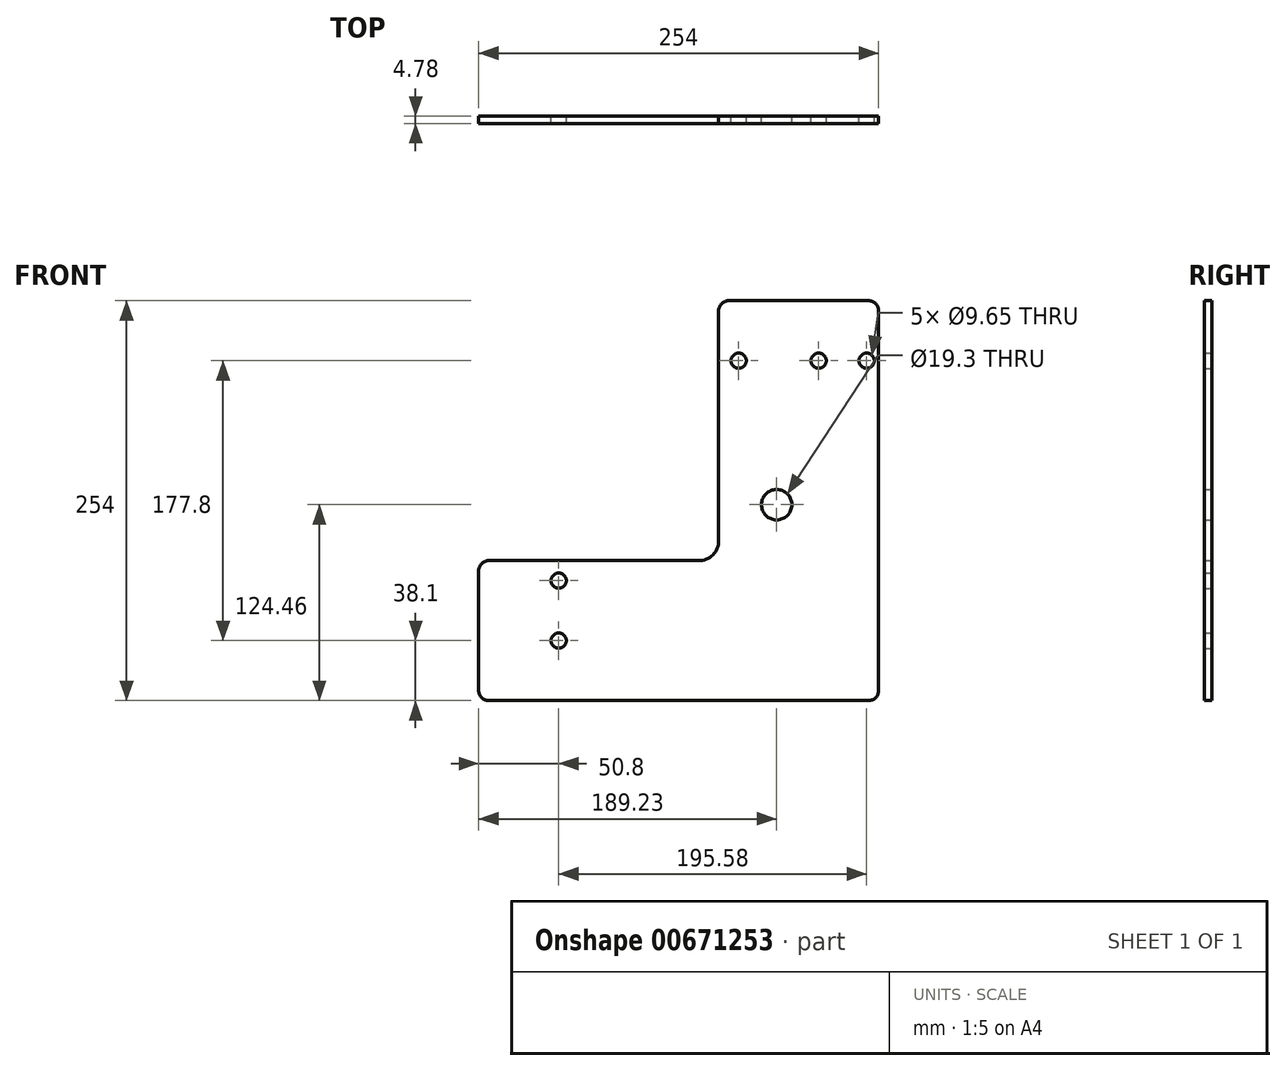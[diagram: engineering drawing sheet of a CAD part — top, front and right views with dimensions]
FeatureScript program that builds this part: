
annotation { "Feature Type Name" : "Feature", "Feature Type Description" : "" }
export const myFeature = defineFeature(function(context is Context, id is Id, definition is map)
    precondition{}
    {
        {
            var Q0;
            Q0=qCreatedBy(makeId("Front.planeOp"),FACE);
            var sketch = newSketch(context, id + "F0", { "sketchPlane" : qUnion([Q0])});
            skPoint(sketch, "E0.middle", {"position": v(0, 0) * mm});
            skLineSegment(sketch, "E1", {"start": v(0, 6.35) * mm, "end": v(0, 247.65) * mm});
            skLineSegment(sketch, "E2", {"start": v(-6.35, 254) * mm, "end": v(-95.25, 254) * mm});
            skLineSegment(sketch, "E3", {"start": v(-101.6, 247.65) * mm, "end": v(-101.6, 101.6) * mm});
            skLineSegment(sketch, "E4", {"start": v(-114.3, 88.9) * mm, "end": v(-247.65, 88.9) * mm});
            skLineSegment(sketch, "E5", {"start": v(-254, 82.55) * mm, "end": v(-254, 6.35) * mm});
            skLineSegment(sketch, "E6", {"start": v(-247.65, 0) * mm, "end": v(-6.35, 0) * mm});
            skCircle(sketch, "E7", {"center": v(-33.35, 48.26) * mm, "radius": 9.53 * mm});
            skCircle(sketch, "E8", {"center": v(-64.77, 124.46) * mm, "radius": 63.5 * mm});
            skPoint(sketch, "E9.visualSharp", {"position": v(-254, 88.9) * mm});
            skArc(sketch, "E9.filletArc", {"start": v(-247.65, 88.9) * mm, "mid": v(-252.14, 87.04) * mm, "end": v(-254, 82.55) * mm});
            skPoint(sketch, "E10.visualSharp", {"position": v(-101.6, 88.9) * mm});
            skArc(sketch, "E10.filletArc", {"start": v(-114.3, 88.9) * mm, "mid": v(-105.32, 92.62) * mm, "end": v(-101.6, 101.6) * mm});
            skPoint(sketch, "E11.visualSharp", {"position": v(-101.6, 254) * mm});
            skArc(sketch, "E11.filletArc", {"start": v(-95.25, 254) * mm, "mid": v(-99.74, 252.14) * mm, "end": v(-101.6, 247.65) * mm});
            skPoint(sketch, "E12.visualSharp", {"position": v(0, 254) * mm});
            skArc(sketch, "E12.filletArc", {"start": v(0, 247.65) * mm, "mid": v(-1.86, 252.14) * mm, "end": v(-6.35, 254) * mm});
            skPoint(sketch, "E13.visualSharp", {"position": v(-254, 0) * mm});
            skArc(sketch, "E13.filletArc", {"start": v(-254, 6.35) * mm, "mid": v(-252.14, 1.86) * mm, "end": v(-247.65, 0) * mm});
            skArc(sketch, "E14.filletArc", {"start": v(-6.35, 0) * mm, "mid": v(-1.86, 1.86) * mm, "end": v(0, 6.35) * mm});
            skCircle(sketch, "E15", {"center": v(-203.2, 76.2) * mm, "radius": 4.83 * mm});
            skCircle(sketch, "E16", {"center": v(-203.2, 38.1) * mm, "radius": 4.83 * mm});
            skCircle(sketch, "E17", {"center": v(-64.77, 124.46) * mm, "radius": 9.65 * mm});
            skCircle(sketch, "E18", {"center": v(-7.62, 215.9) * mm, "radius": 4.83 * mm});
            skCircle(sketch, "E19", {"center": v(-38.1, 215.9) * mm, "radius": 4.83 * mm});
            skCircle(sketch, "E20", {"center": v(-88.9, 215.9) * mm, "radius": 4.83 * mm});
            skSolve(sketch);
        }
        {
            var Q0;
            Q0=makeQuery(id+"F0.imprint","IMPRINT",FACE,{"disambiguationData":[TD([[makeQuery(id+"F0.imprint","IMPRINT",EDGE,{"derivedFrom":sQuery(id+"F0.wireOp",EDGE,"E1")}),1.0]])]});
            var Q1;
            Q1=makeQuery(id+"F0.imprint","IMPRINT",FACE,{"disambiguationData":[TD([[makeQuery(id+"F0.imprint","IMPRINT",EDGE,{"derivedFrom":sQuery(id+"F0.wireOp",EDGE,"E7")}),1.0]])]});
            var Q2;
            {var subQ0=sQuery(id+"F0.wireOp",EDGE,"E10.filletArc");Q2=makeQuery(id+"F0.imprint","IMPRINT",FACE,{"disambiguationData":[TD([[makeQuery(id+"F0.imprint","IMPRINT",EDGE,{"derivedFrom":subQ0}),-1.0]])]});}
            extrude(context, id + "F1", {"entities" : qUnion([Q0, Q1, Q2]), "depth" : 4.78 * mm, "offsetDistance" : 25.4 * mm});
        }
    });
